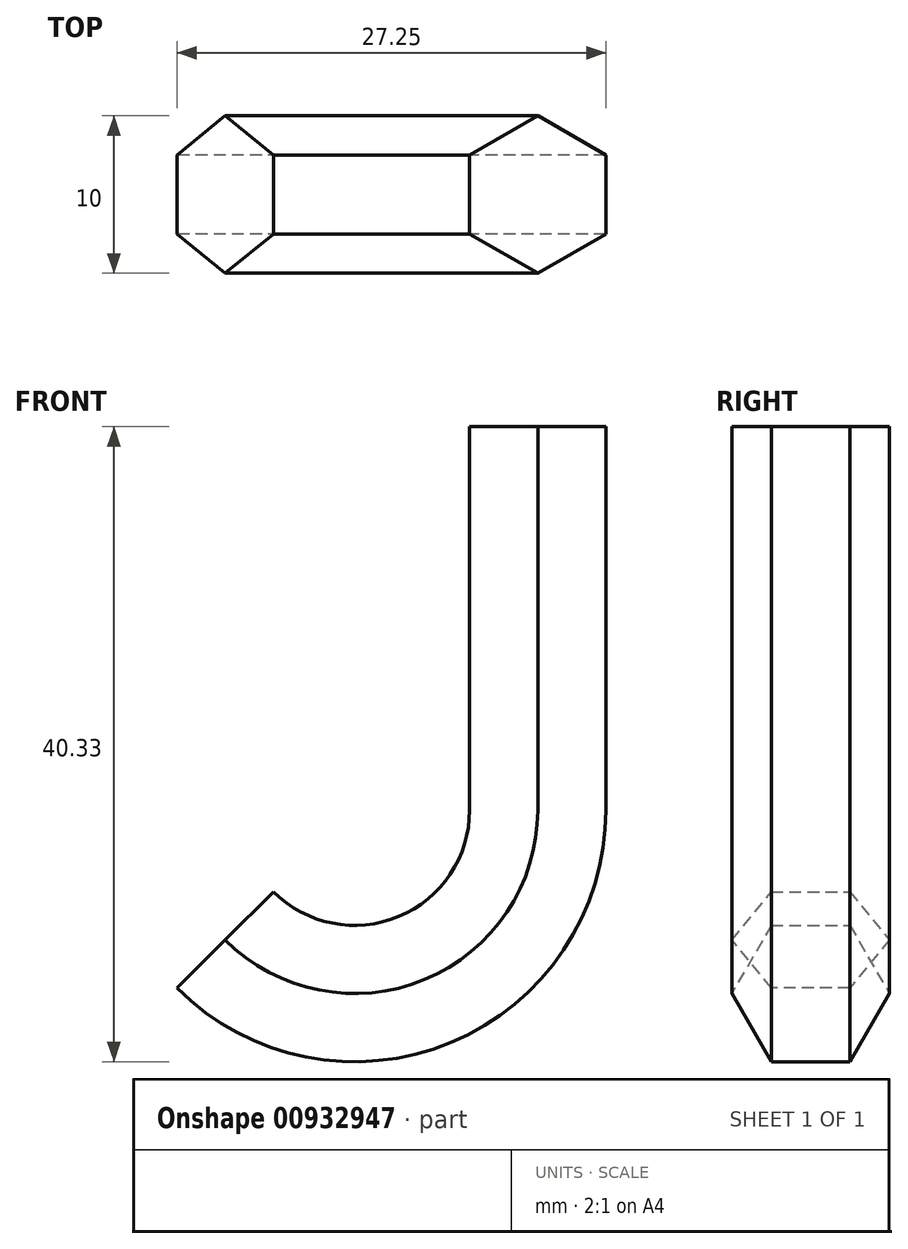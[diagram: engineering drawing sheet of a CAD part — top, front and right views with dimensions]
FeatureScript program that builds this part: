
annotation { "Feature Type Name" : "Feature", "Feature Type Description" : "" }
export const myFeature = defineFeature(function(context is Context, id is Id, definition is map)
    precondition{}
    {
        {
            var Q0;
            Q0=qCreatedBy(makeId("Front.planeOp"),FACE);
            var sketch = newSketch(context, id + "F0", { "sketchPlane" : qUnion([Q0])});
            skLineSegment(sketch, "E0", {"start": v(0, 0) * mm, "end": v(0, -24.37) * mm});
            skArc(sketch, "E1", {"start": v(-19.85, -32.6) * mm, "mid": v(-7.18, -35.12) * mm, "end": v(0, -24.37) * mm});
            skLineSegment(sketch, "E2", {"start": v(-11.63, -24.37) * mm, "end": v(-19.85, -32.6) * mm, "construction": true});
            skLineSegment(sketch, "E3", {"start": v(-11.63, -24.37) * mm, "end": v(0, -24.37) * mm, "construction": true});
            skSolve(sketch);
        }
        {
            var Q0;
            Q0=qCreatedBy(makeId("Top.planeOp"),FACE);
            var sketch = newSketch(context, id + "F1", { "sketchPlane" : qUnion([Q0])});
            skCircle(sketch, "E4.cCircle", {"center": v(0, 0) * mm, "radius": 5 * mm, "construction": true});
            skLineSegment(sketch, "E4.0", {"start": v(0, -5) * mm, "end": v(-4.33, -2.5) * mm});
            skLineSegment(sketch, "E4.1", {"start": v(-4.33, -2.5) * mm, "end": v(-4.33, 2.5) * mm});
            skLineSegment(sketch, "E4.2", {"start": v(-4.33, 2.5) * mm, "end": v(0, 5) * mm});
            skLineSegment(sketch, "E4.3", {"start": v(0, 5) * mm, "end": v(4.33, 2.5) * mm});
            skLineSegment(sketch, "E4.4", {"start": v(4.33, 2.5) * mm, "end": v(4.33, -2.5) * mm});
            skLineSegment(sketch, "E4.5", {"start": v(4.33, -2.5) * mm, "end": v(0, -5) * mm});
            skSolve(sketch);
        }
        {
            var Q0;
            Q0=makeQuery(id+"F1.imprint","IMPRINT",FACE,{"disambiguationData":[TD([[makeQuery(id+"F1.imprint","IMPRINT",EDGE,{"derivedFrom":sQuery(id+"F1.wireOp",EDGE,"E4.0")}),-1.0]])]});
            var Q1;
            Q1=sQuery(id+"F0.wireOp",EDGE,"E0");
            var Q2;
            Q2=sQuery(id+"F0.wireOp",EDGE,"E1");
            sweep(context, id + "F2", {"profiles" : qUnion([Q0]), "path" : qUnion([Q1, Q2])});
        }
    });
